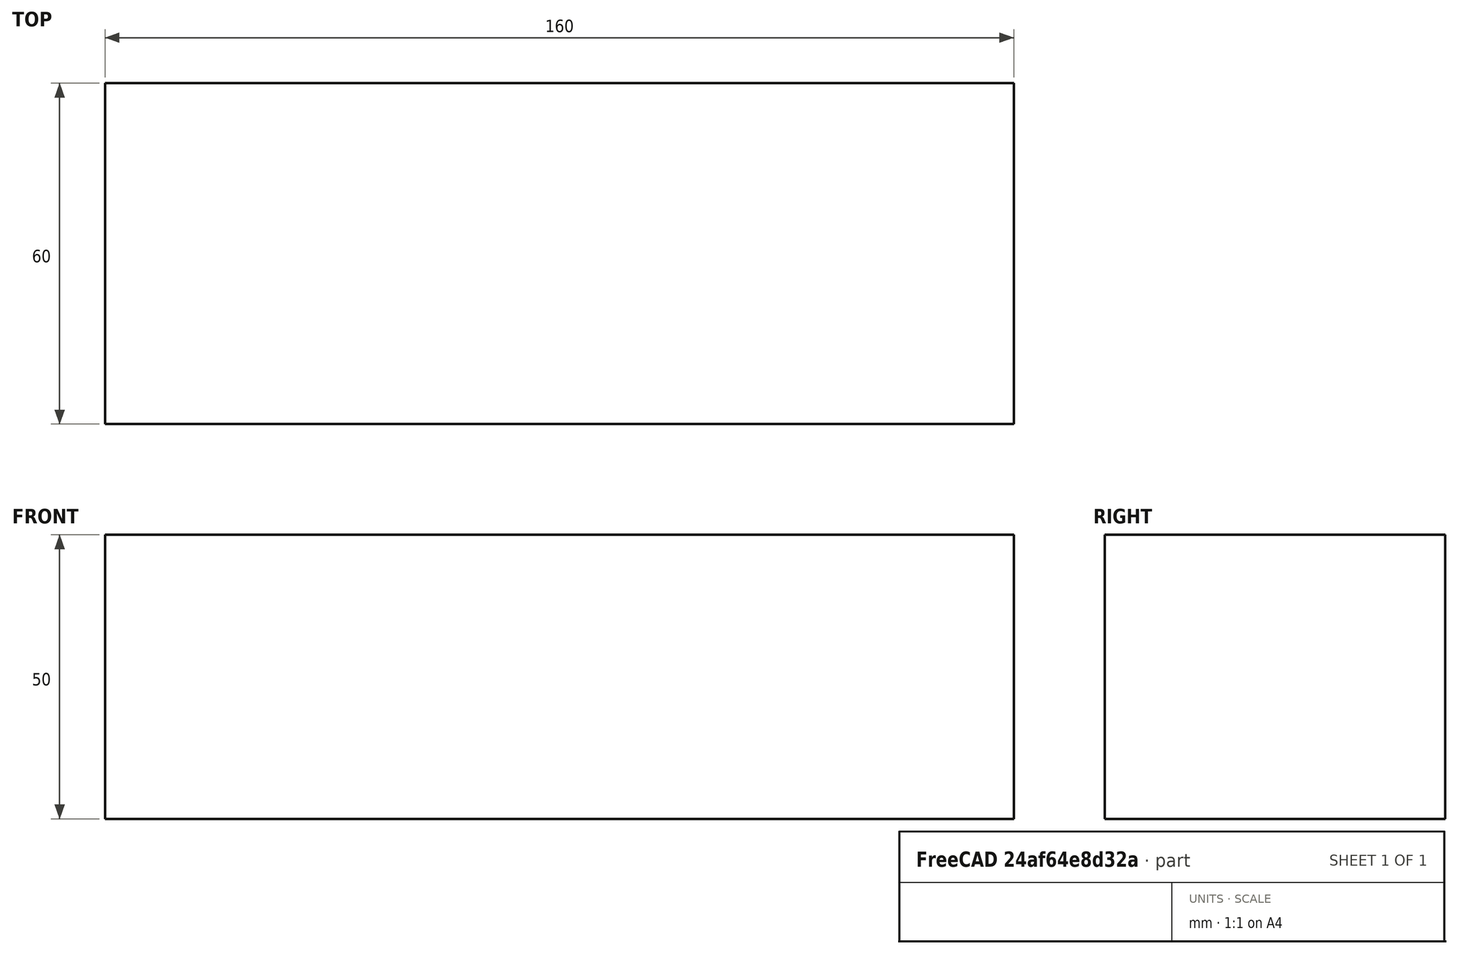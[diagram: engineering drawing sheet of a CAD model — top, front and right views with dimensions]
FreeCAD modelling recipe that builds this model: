
FCSTD DOCUMENT  (FreeCAD 0.15R4671 (Git))
Label: Flat Bar 160x60 EN10058 S235JR
License: All rights reserved
LicenseURL: http://en.wikipedia.org/wiki/All_rights_reserved
objects: Sketcher::SketchObject×1, Part::Extrusion×1
note: 2 computed .brp shape members not serialized (recipe doc carries the construction recipe); baked Part::Feature solids carry a one-line shape summary decoded from their .brp

FEATURE [Sketcher::SketchObject] Sketch
  sketch-geometry (4):
    g0: LineSegment StartX=-80 StartY=-30 StartZ=0 EndX=80 EndY=-30 EndZ=0
    g1: LineSegment StartX=80 StartY=-30 StartZ=0 EndX=80 EndY=30 EndZ=0
    g2: LineSegment StartX=80 StartY=30 StartZ=0 EndX=-80 EndY=30 EndZ=0
    g3: LineSegment StartX=-80 StartY=30 StartZ=0 EndX=-80 EndY=-30 EndZ=0
  constraints (12):
    c: Coincident(g0,g1)
    c: Coincident(g1,g2)
    c: Coincident(g2,g3)
    c: Coincident(g3,g0)
    c: Horizontal(g0)
    c: Horizontal(g2)
    c: Vertical(g1)
    c: Vertical(g3)
    c: Symmetric(g1,g2,g-2)
    c: Symmetric(g0,g1,g-1)
    c: DistanceY(g1) = 60
    c: DistanceX(g0) = 160
FEATURE [Part::Extrusion] Extrude  label="Flat Bar 160x60 EN10058 S235JR"
  Base = -> Sketch
  Dir = (0,0,50)
  Solid = true
